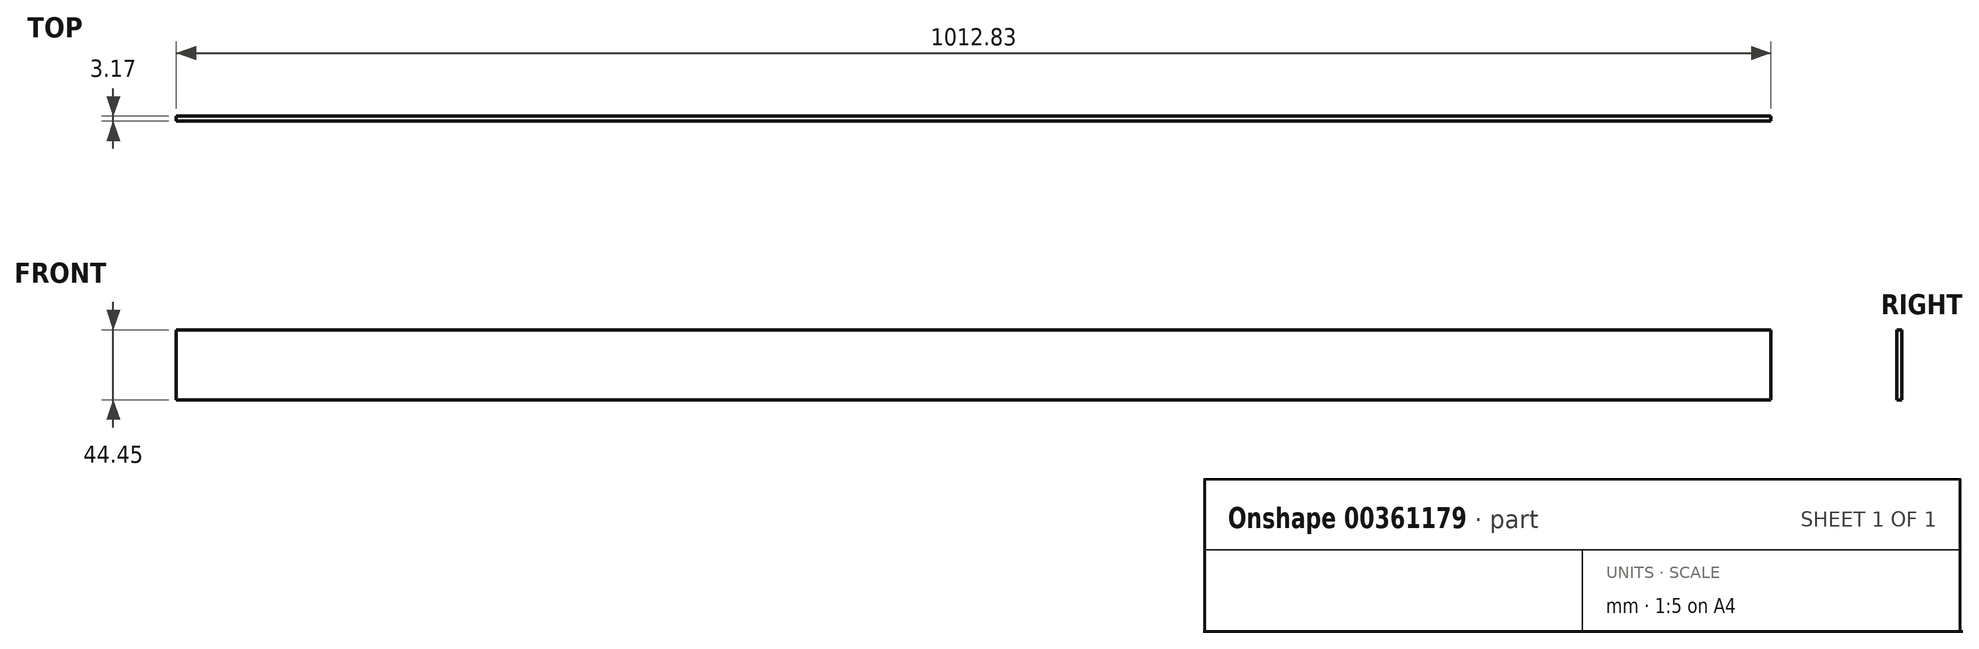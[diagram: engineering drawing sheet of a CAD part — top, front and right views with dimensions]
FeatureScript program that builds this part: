
annotation { "Feature Type Name" : "Feature", "Feature Type Description" : "" }
export const myFeature = defineFeature(function(context is Context, id is Id, definition is map)
    precondition{}
    {
        {
            var Q0;
            Q0=qCreatedBy(makeId("Front.planeOp"),FACE);
            var sketch = newSketch(context, id + "F0", { "sketchPlane" : qUnion([Q0])});
            skLineSegment(sketch, "E0", {"start": v(0, 0) * mm, "end": v(0, 44.45) * mm});
            skLineSegment(sketch, "E1", {"start": v(0, 44.45) * mm, "end": v(1012.83, 44.45) * mm});
            skLineSegment(sketch, "E2", {"start": v(1012.83, 44.45) * mm, "end": v(1012.83, 0) * mm});
            skLineSegment(sketch, "E3", {"start": v(1012.82, 0) * mm, "end": v(0, 0) * mm});
            skSolve(sketch);
        }
        {
            var Q0;
            Q0=makeQuery(id+"F0.imprint","IMPRINT",FACE,{"disambiguationData":[TD([[makeQuery(id+"F0.imprint","IMPRINT",EDGE,{"derivedFrom":sQuery(id+"F0.wireOp",EDGE,"E0")}),-1.0]])]});
            extrude(context, id + "F1", {"entities" : qUnion([Q0]), "depth" : 3.17 * mm});
        }
    });
